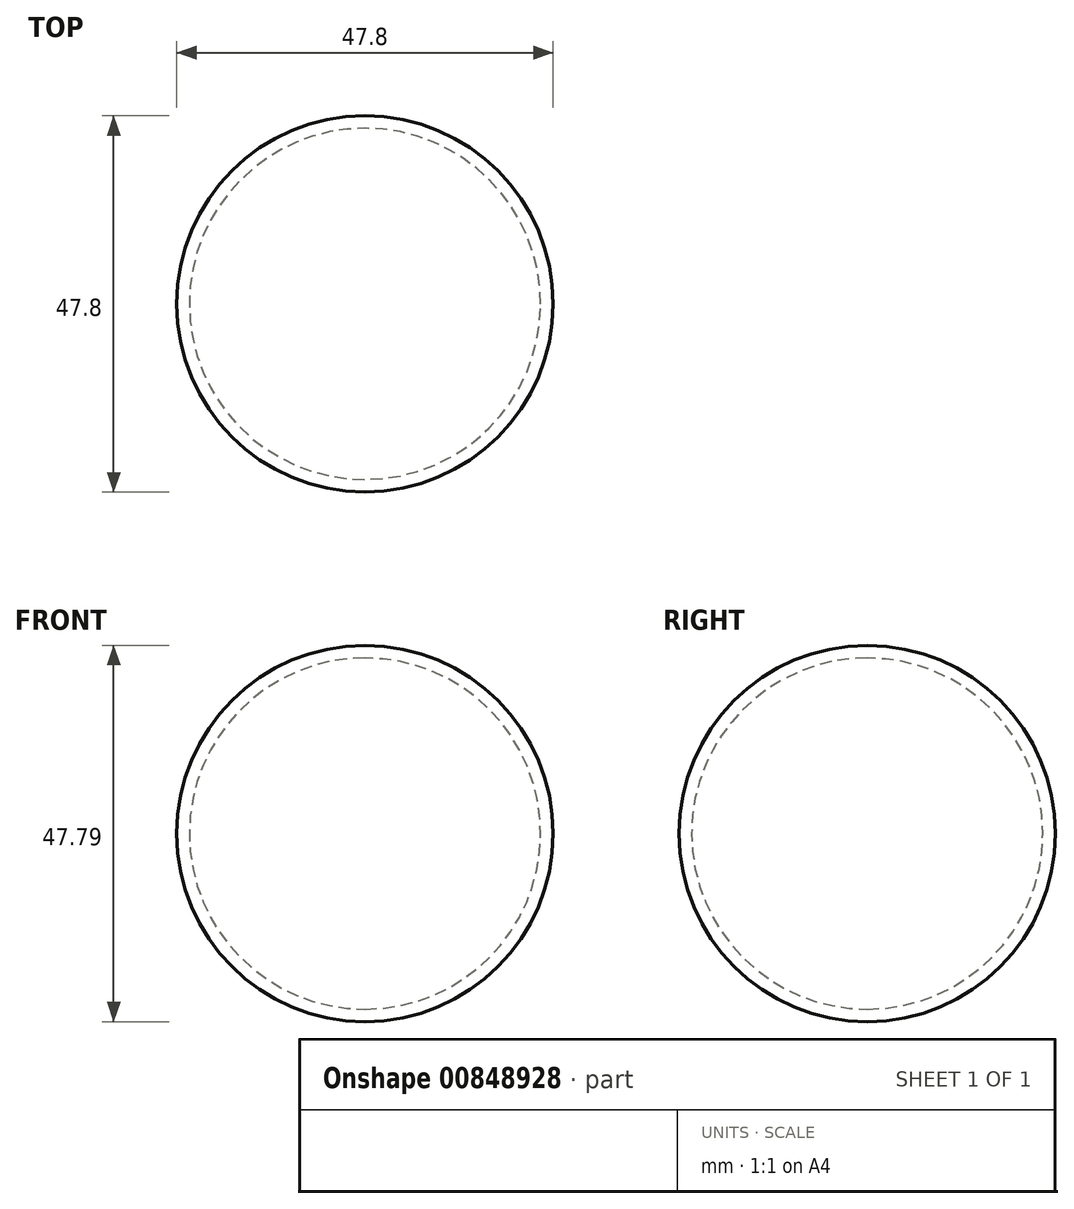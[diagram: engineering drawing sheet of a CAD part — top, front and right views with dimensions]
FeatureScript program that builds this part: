
annotation { "Feature Type Name" : "Feature", "Feature Type Description" : "" }
export const myFeature = defineFeature(function(context is Context, id is Id, definition is map)
    precondition{}
    {
        {
            var Q0;
            Q0=qCreatedBy(makeId("Front.planeOp"),FACE);
            var sketch = newSketch(context, id + "F0", { "sketchPlane" : qUnion([Q0])});
            skLineSegment(sketch, "E0", {"start": v(0, 0) * mm, "end": v(0, 0) * mm});
            skLineSegment(sketch, "E1", {"start": v(0, 0) * mm, "end": v(0, 44.6) * mm});
            skArc(sketch, "E2", {"start": v(0, 0) * mm, "mid": v(22.3, 22.3) * mm, "end": v(0, 44.6) * mm});
            skPoint(sketch, "E3.orphan", {"position": v(0, 61.55) * mm});
            skLineSegment(sketch, "E4", {"start": v(0, 44.6) * mm, "end": v(0, 61.55) * mm});
            skLineSegment(sketch, "E5", {"start": v(0, 0) * mm, "end": v(0, -4.75) * mm});
            skArc(sketch, "E6.0", {"start": v(0, -1.6) * mm, "mid": v(23.9, 22.3) * mm, "end": v(0, 46.2) * mm});
            skLineSegment(sketch, "E6.1", {"start": v(0, -1.6) * mm, "end": v(0, -1.6) * mm});
            skLineSegment(sketch, "E7", {"start": v(0, 46.2) * mm, "end": v(0, 44.6) * mm});
            skLineSegment(sketch, "E8", {"start": v(0, 0) * mm, "end": v(0, -1.6) * mm});
            skLineSegment(sketch, "E9", {"start": v(0, 0) * mm, "end": v(0, 70.08) * mm});
            skSolve(sketch);
        }
        {
            var Q0;
            Q0=makeQuery(id+"F0.imprint","IMPRINT",FACE,{"disambiguationData":[TD([[makeQuery(id+"F0.imprint","IMPRINT",EDGE,{"derivedFrom":sQuery(id+"F0.wireOp",EDGE,"E6.0")}),1.0]])]});
            var Q1;
            {var subQ1=sQuery(id+"F0.wireOp",EDGE,"E0");Q1=makeQuery(id+"F0.imprint","IMPRINT",FACE,{"disambiguationData":[TD([[makeQuery(id+"F0.imprint","IMPRINT",EDGE,{"derivedFrom":subQ1}),1.0]])]});}
            var Q2;
            Q2=sQuery(id+"F0.wireOp",EDGE,"E9");
            revolve(context, id + "F1", {"surfaceOperationType" : NewSurfaceOperationType.NEW, "entities" : qUnion([Q0, Q1]), "axis" : qUnion([Q2]), "revolveType" : RevolveType.FULL});
        }
    });
